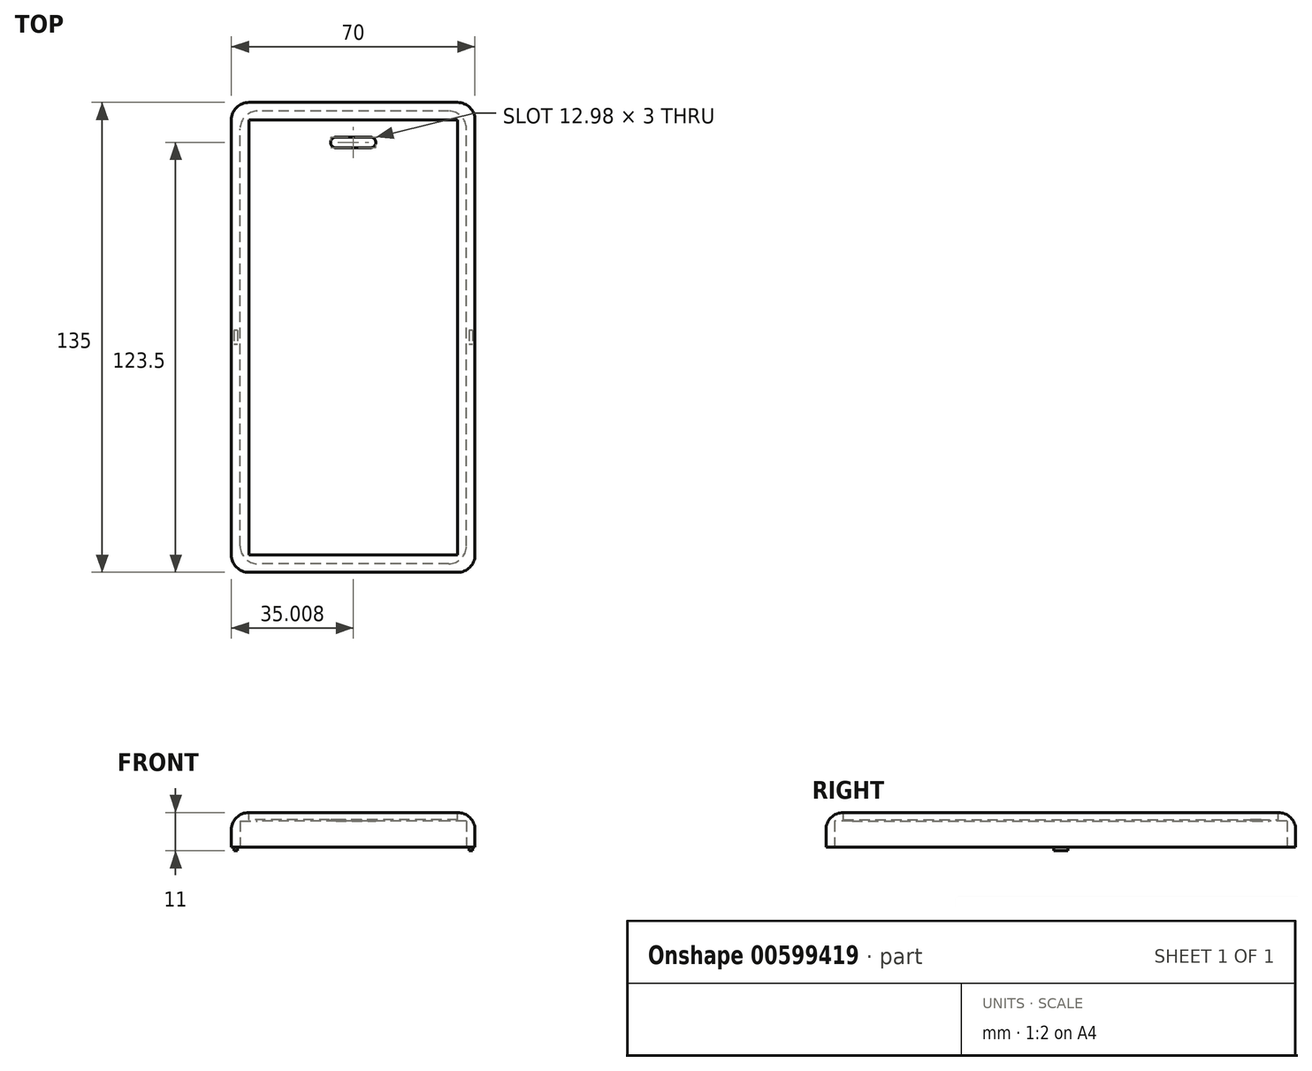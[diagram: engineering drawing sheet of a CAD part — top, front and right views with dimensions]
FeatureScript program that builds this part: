
annotation { "Feature Type Name" : "Feature", "Feature Type Description" : "" }
export const myFeature = defineFeature(function(context is Context, id is Id, definition is map)
    precondition{}
    {
        {
            var Q0;
            Q0=qCreatedBy(makeId("Top.planeOp"),FACE);
            var sketch = newSketch(context, id + "F0", { "sketchPlane" : qUnion([Q0])});
            skLineSegment(sketch, "E0.bottom", {"start": v(35, -67.5) * mm, "end": v(-35, -67.5) * mm});
            skLineSegment(sketch, "E0.top", {"start": v(35, 67.5) * mm, "end": v(-35, 67.5) * mm});
            skLineSegment(sketch, "E0.left", {"start": v(35, -67.5) * mm, "end": v(35, 67.5) * mm});
            skLineSegment(sketch, "E0.right", {"start": v(-35, -67.5) * mm, "end": v(-35, 67.5) * mm});
            skPoint(sketch, "E0.middle", {"position": v(0, 0) * mm});
            skSolve(sketch);
        }
        {
            var Q0;
            Q0=makeQuery(id+"F0.imprint","IMPRINT",FACE,{"disambiguationData":[TD([[makeQuery(id+"F0.imprint","IMPRINT",EDGE,{"derivedFrom":sQuery(id+"F0.wireOp",EDGE,"E0.bottom")}),-1.0]])]});
            extrude(context, id + "F1", {"entities" : qUnion([Q0]), "depth" : 10 * mm, "offsetDistance" : 25 * mm});
        }
        {
            var Q0;
            Q0=makeQuery(id+"F1.opExtrude","CAP_FACE",FACE,{"disambiguationData":[OSD([sQuery(id+"F0.wireOp",EDGE,"E0.bottom"),sQuery(id+"F0.wireOp",EDGE,"E0.top"),sQuery(id+"F0.wireOp",EDGE,"E0.left"),sQuery(id+"F0.wireOp",EDGE,"E0.right")])],"isStart":true});
            var Q1;
            Q1=makeQuery(id+"F1.opExtrude","SWEPT_BODY",BODY,{"disambiguationData":[OSD([sQuery(id+"F0.wireOp",EDGE,"E0.bottom"),sQuery(id+"F0.wireOp",EDGE,"E0.top"),sQuery(id+"F0.wireOp",EDGE,"E0.left"),sQuery(id+"F0.wireOp",EDGE,"E0.right")])]});
            shell(context, id + "F2", {"entities" : qUnion([Q0]), "parts" : qUnion([Q1]), "thickness" : 2.5 * mm});
        }
        {
            var Q0;
            Q0=makeQuery(id+"F1.opExtrude","CAP_EDGE",EDGE,{"disambiguationData":[OSD([sQuery(id+"F0.wireOp",EDGE,"E0.top")])],"isStart":false});
            var Q1;
            Q1=makeQuery(id+"F1.opExtrude","CAP_EDGE",EDGE,{"disambiguationData":[OSD([sQuery(id+"F0.wireOp",EDGE,"E0.left")])],"isStart":false});
            var Q2;
            Q2=makeQuery(id+"F1.opExtrude","SWEPT_EDGE",EDGE,{"disambiguationData":[OSD([sQuery(id+"F0.wireOp",EDGE,"E0.top"),sQuery(id+"F0.wireOp",EDGE,"E0.left")])]});
            fillet(context, id + "F3", {"entities" : qUnion([Q0, Q1, Q2]), "radius" : 5 * mm, "tangentPropagation" : true, "allowEdgeOverflow" : false});
        }
        {
            var Q0;
            Q0=makeQuery(id+"F3.opFillet","BLEND_EDGE",EDGE,{"blendedFrom":[makeQuery(id+"F1.opExtrude","CAP_EDGE",EDGE,{"disambiguationData":[OSD([sQuery(id+"F0.wireOp",EDGE,"E0.left")])],"isStart":false}),makeQuery(id+"F1.opExtrude","SWEPT_FACE",FACE,{"disambiguationData":[OSD([sQuery(id+"F0.wireOp",EDGE,"E0.bottom")])]})],"blendedInto":[makeQuery(id+"F1.opExtrude","SWEPT_FACE",FACE,{"disambiguationData":[OSD([sQuery(id+"F0.wireOp",EDGE,"E0.bottom")])]})]});
            var Q1;
            Q1=makeQuery(id+"F1.opExtrude","CAP_EDGE",EDGE,{"disambiguationData":[OSD([sQuery(id+"F0.wireOp",EDGE,"E0.bottom")])],"isStart":false});
            fillet(context, id + "F4", {"entities" : qUnion([Q0, Q1]), "radius" : 5 * mm, "tangentPropagation" : true, "allowEdgeOverflow" : false});
        }
        {
            var Q0;
            Q0=makeQuery(id+"F1.opExtrude","CAP_EDGE",EDGE,{"disambiguationData":[OSD([sQuery(id+"F0.wireOp",EDGE,"E0.right")])],"isStart":false});
            var Q1;
            Q1=makeQuery(id+"F4.opFillet","BLEND_EDGE",EDGE,{"blendedFrom":[makeQuery(id+"F1.opExtrude","CAP_EDGE",EDGE,{"disambiguationData":[OSD([sQuery(id+"F0.wireOp",EDGE,"E0.bottom")])],"isStart":false}),makeQuery(id+"F1.opExtrude","SWEPT_FACE",FACE,{"disambiguationData":[OSD([sQuery(id+"F0.wireOp",EDGE,"E0.right")])]})],"blendedInto":[makeQuery(id+"F1.opExtrude","SWEPT_FACE",FACE,{"disambiguationData":[OSD([sQuery(id+"F0.wireOp",EDGE,"E0.right")])]})]});
            fillet(context, id + "F5", {"entities" : qUnion([Q0, Q1]), "radius" : 5 * mm, "tangentPropagation" : true, "allowEdgeOverflow" : false});
        }
        {
            var Q0;
            Q0=makeQuery(id+"F2.opShell","OFFSET_EDGE",EDGE,{"disambiguationData":[OSD([sQuery(id+"F0.wireOp",EDGE,"E0.top"),sQuery(id+"F0.wireOp",EDGE,"E0.left")])]});
            var Q1;
            Q1=makeQuery(id+"F2.opShell","OFFSET_EDGE",EDGE,{"disambiguationData":[OSD([sQuery(id+"F0.wireOp",EDGE,"E0.top"),sQuery(id+"F0.wireOp",EDGE,"E0.right")])]});
            var Q2;
            Q2=makeQuery(id+"F2.opShell","OFFSET_EDGE",EDGE,{"disambiguationData":[OSD([sQuery(id+"F0.wireOp",EDGE,"E0.bottom"),sQuery(id+"F0.wireOp",EDGE,"E0.left")])]});
            var Q3;
            Q3=makeQuery(id+"F2.opShell","OFFSET_EDGE",EDGE,{"disambiguationData":[OSD([sQuery(id+"F0.wireOp",EDGE,"E0.bottom"),sQuery(id+"F0.wireOp",EDGE,"E0.right")])]});
            fillet(context, id + "F6", {"entities" : qUnion([Q0, Q1, Q2, Q3]), "radius" : 5 * mm, "tangentPropagation" : true, "allowEdgeOverflow" : false});
        }
        {
            var Q0;
            Q0=makeQuery(id+"F1.opExtrude","CAP_FACE",FACE,{"disambiguationData":[OSD([sQuery(id+"F0.wireOp",EDGE,"E0.bottom"),sQuery(id+"F0.wireOp",EDGE,"E0.top"),sQuery(id+"F0.wireOp",EDGE,"E0.left"),sQuery(id+"F0.wireOp",EDGE,"E0.right")])],"isStart":true});
            var sketch = newSketch(context, id + "F7", { "sketchPlane" : qUnion([Q0])});
            skLineSegment(sketch, "E1.bottom", {"start": v(34.25, -2) * mm, "end": v(33.25, -2) * mm});
            skLineSegment(sketch, "E1.top", {"start": v(34.25, 2) * mm, "end": v(33.25, 2) * mm});
            skLineSegment(sketch, "E1.left", {"start": v(34.25, -2) * mm, "end": v(34.25, 2) * mm});
            skLineSegment(sketch, "E1.right", {"start": v(33.25, -2) * mm, "end": v(33.25, 2) * mm});
            skPoint(sketch, "E1.middle", {"position": v(33.75, 0) * mm});
            skLineSegment(sketch, "E2.bottom", {"start": v(-33.25, -2) * mm, "end": v(-34.25, -2) * mm});
            skLineSegment(sketch, "E2.top", {"start": v(-33.25, 2) * mm, "end": v(-34.25, 2) * mm});
            skLineSegment(sketch, "E2.left", {"start": v(-33.25, -2) * mm, "end": v(-33.25, 2) * mm});
            skLineSegment(sketch, "E2.right", {"start": v(-34.25, -2) * mm, "end": v(-34.25, 2) * mm});
            skPoint(sketch, "E2.middle", {"position": v(-33.75, 0) * mm});
            skSolve(sketch);
        }
        {
            var Q0;
            Q0=makeQuery(id+"F7.imprint","IMPRINT",FACE,{"disambiguationData":[TD([[makeQuery(id+"F7.imprint","IMPRINT",EDGE,{"derivedFrom":sQuery(id+"F7.wireOp",EDGE,"E2.bottom")}),-1.0]])]});
            var Q1;
            Q1=makeQuery(id+"F7.imprint","IMPRINT",FACE,{"disambiguationData":[TD([[makeQuery(id+"F7.imprint","IMPRINT",EDGE,{"derivedFrom":sQuery(id+"F7.wireOp",EDGE,"E1.bottom")}),-1.0]])]});
            extrude(context, id + "F8", {"entities" : qUnion([Q0, Q1]), "operationType" : NewBodyOperationType.ADD, "depth" : 1 * mm, "offsetDistance" : 25 * mm});
        }
        {
            var Q0;
            Q0=makeQuery(id+"F1.opExtrude","CAP_FACE",FACE,{"disambiguationData":[OSD([sQuery(id+"F0.wireOp",EDGE,"E0.bottom"),sQuery(id+"F0.wireOp",EDGE,"E0.top"),sQuery(id+"F0.wireOp",EDGE,"E0.left"),sQuery(id+"F0.wireOp",EDGE,"E0.right")])],"isStart":false});
            extrude(context, id + "F9", {"entities" : qUnion([Q0]), "operationType" : NewBodyOperationType.REMOVE, "oppositeDirection" : true, "depth" : 2 * mm, "offsetDistance" : 25 * mm});
        }
        {
            var Q0;
            Q0=makeQuery(id+"F9.boolean.opBoolean","COPY",FACE,{"derivedFrom":makeQuery(id+"F9.opExtrude","CAP_FACE",FACE,{"disambiguationData":[OSD([sQuery(id+"F0.wireOp",EDGE,"E0.bottom"),sQuery(id+"F0.wireOp",EDGE,"E0.top"),sQuery(id+"F0.wireOp",EDGE,"E0.left"),sQuery(id+"F0.wireOp",EDGE,"E0.right")])],"isStart":false})});
            var sketch = newSketch(context, id + "F10", { "sketchPlane" : qUnion([Q0])});
            skLineSegment(sketch, "E3", {"start": v(0, 62.5) * mm, "end": v(0, 57.5) * mm});
            skPoint(sketch, "E3.endSnap0", {"position": v(0, 62.5) * mm});
            skLineSegment(sketch, "E4", {"start": v(0, 57.5) * mm, "end": v(5, 57.5) * mm});
            skLineSegment(sketch, "E5", {"start": v(0, 57.5) * mm, "end": v(-4.98, 57.5) * mm});
            skLineSegment(sketch, "E6", {"start": v(-4.98, 54.5) * mm, "end": v(5.03, 54.5) * mm});
            skArc(sketch, "E7", {"start": v(-4.98, 57.5) * mm, "mid": v(-6.48, 56) * mm, "end": v(-4.98, 54.5) * mm});
            skArc(sketch, "E8", {"start": v(5.03, 54.5) * mm, "mid": v(6.5, 56.01) * mm, "end": v(5, 57.5) * mm});
            skSolve(sketch);
        }
        {
            var Q0;
            Q0=makeQuery(id+"F10.imprint","IMPRINT",FACE,{"disambiguationData":[TD([[makeQuery(id+"F10.imprint","IMPRINT",EDGE,{"derivedFrom":sQuery(id+"F10.wireOp",EDGE,"E4")}),-1.0]])]});
            extrude(context, id + "F11", {"entities" : qUnion([Q0]), "operationType" : NewBodyOperationType.REMOVE, "oppositeDirection" : true, "depth" : 1 * mm, "offsetDistance" : 25 * mm});
        }
    });
